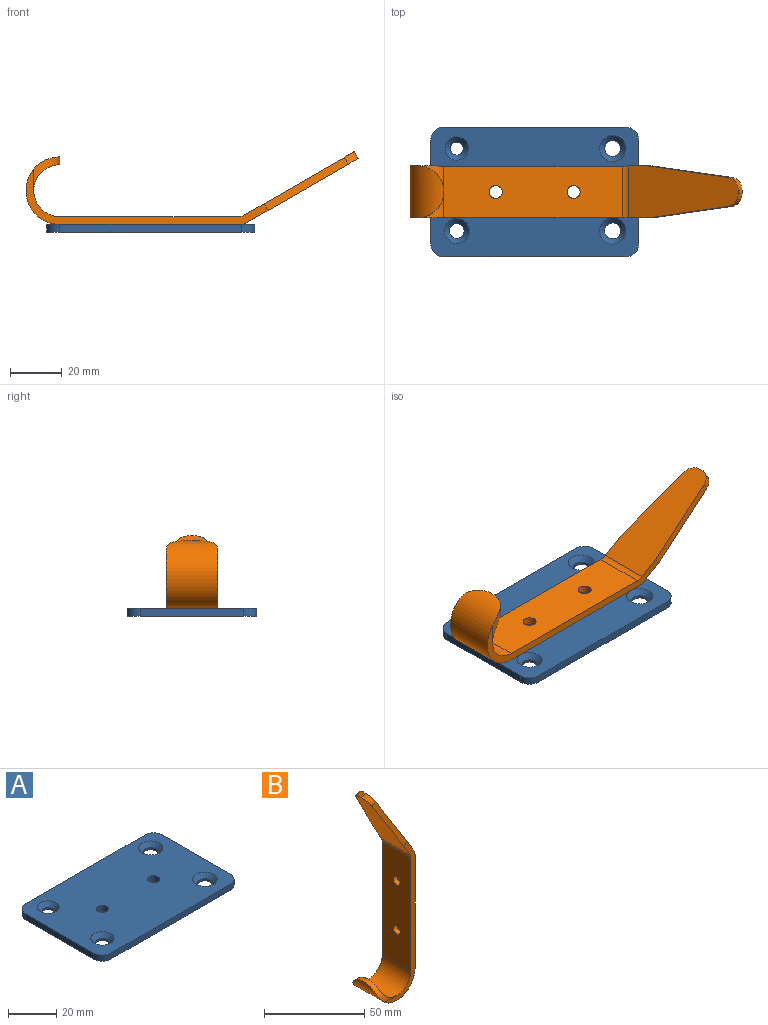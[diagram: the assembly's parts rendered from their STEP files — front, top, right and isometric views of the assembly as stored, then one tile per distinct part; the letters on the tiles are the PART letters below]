
ASSEMBLY  parts=2 mates=1
PART A: 20 faces, bbox 80x50x3 mm
  f0: plane 70x3mm, normal (0,1,0), area 210mm2, adj f4,f5,f6,f9
  f1: plane 40x3mm, normal (-1,0,0), area 120mm2, adj f4,f5,f6,f7
  f2: plane 70x3mm, normal (0,-1,0), area 210mm2, adj f4,f5,f7,f8
  f3: plane 40x3mm, normal (1,0,0), area 120mm2, adj f4,f5,f8,f9
  f4: plane 80x50mm, normal (0,0,1), area 3641.3mm2, adj f0,f1,f2,f3,f6,f7,f8,f9
  f5: plane 80x50mm, normal (0,0,-1), area 3835.5mm2, adj f0,f1,f2,f3,f6,f7,f8,f9
  f6: cylinder r=5mm len=5mm, axis (0,0,1), area 23.6mm2, adj f0,f1,f4,f5
  f7: cylinder r=5mm len=5mm, axis (0,0,-1), area 23.6mm2, adj f1,f2,f4,f5
  f8: cylinder r=5mm len=5mm, axis (0,0,1), area 23.6mm2, adj f2,f3,f4,f5
  f9: cylinder r=5mm len=5mm, axis (0,0,-1), area 23.6mm2, adj f0,f3,f4,f5
  f10: cylinder r=2.5mm len=5mm, axis (0,0,1), area 15.7mm2, adj f5,f17
  f11: cylinder r=3.08mm len=6.17mm, axis (0,0,1), area 19.4mm2, adj f5,f15
  f12: cylinder r=3.04mm len=6.08mm, axis (0,0,1), area 19.1mm2, adj f5,f14
  f13: cylinder r=2.83mm len=5.67mm, axis (0,0,1), area 17.8mm2, adj f5,f16
  f14: cone r=3.04mm half-angle=45deg, axis (0,0,1), area 71.8mm2, adj f4,f12
  f15: cone r=3.08mm half-angle=45deg, axis (0,0,1), area 72.6mm2, adj f4,f11
  f16: cone r=2.83mm half-angle=45deg, axis (0,0,1), area 68.1mm2, adj f4,f13
  f17: cone r=2.5mm half-angle=45deg, axis (0,0,1), area 62.2mm2, adj f4,f10
  f18: cylinder r=2.5mm len=5mm, axis (0,0,1), area 47.1mm2, adj f4,f5
  f19: cylinder r=2.5mm len=5mm, axis (0,0,1), area 47.1mm2, adj f4,f5
PART B: 18 faces, bbox 28x20x127.8 mm
  f0: cylinder r=13mm len=26mm, axis (0,1,0), area 772.6mm2, adj f1,f7,f8,f9
  f1: plane 69.46x20mm, normal (1,0,0), area 1350mm2, adj f0,f7,f8,f14,f15,f16
  f2: plane 42.84x24.73mm, normal (0.87,0,0.5), area 781.3mm2, adj f3,f7,f8,f10,f11,f12,f13,f16
  f3: plane 2.6x1.5mm, normal (-0.5,0,0.87), area 3.5mm2, adj f2,f4,f12,f13
  f4: plane 42.14x24.33mm, normal (-0.87,0,-0.5), area 765.2mm2, adj f3,f7,f8,f10,f11,f12,f13,f17
  f5: plane 68.66x20mm, normal (-1,0,0), area 1333.9mm2, adj f6,f7,f8,f14,f15,f17
  f6: cylinder r=10mm len=20mm, axis (0,1,0), area 582.9mm2, adj f5,f7,f8,f9
  f7: plane 93.16x21.31mm, normal (0,-1,0), area 313.6mm2, adj f0,f1,f2,f4,f5,f6,f9,f10
  f8: plane 93.16x21.31mm, normal (0,1,0), area 313.6mm2, adj f0,f1,f2,f4,f5,f6,f9,f11
  f9: cylinder r=10mm len=20mm, axis (1,0,0), area 109.2mm2, adj f0,f6,f7,f8
  f10: plane 32.35x20.41mm, normal (-0.06,-0.99,0.11), area 107.7mm2, adj f2,f4,f7,f12
  f11: plane 32.35x20.41mm, normal (-0.06,0.99,0.11), area 107.7mm2, adj f2,f4,f8,f13
  f12: cylinder r=5mm len=5.29mm, axis (-0.87,0,-0.5), area 21.7mm2, adj f2,f3,f4,f10
  f13: cylinder r=5mm len=5.29mm, axis (-0.87,0,-0.5), area 21.7mm2, adj f2,f3,f4,f11
  f14: cylinder r=2.5mm len=5mm, axis (-1,0,0), area 47.1mm2, adj f1,f5
  f15: cylinder r=2.5mm len=5mm, axis (-1,0,0), area 47.1mm2, adj f1,f5
  f16: cylinder r=5mm len=20mm, axis (0,1,0), area 52.4mm2, adj f1,f2,f7,f8
  f17: cylinder r=5mm len=20mm, axis (0,-1,0), area 52.4mm2, adj f4,f5,f7,f8
PLACE A t=(5.22,10.84,11.53)mm
PLACE B rot(axis=(0,1,0),90deg) t=(-30,21.58,27.53)mm
MATE fastened B.f15 <-> A.f18  axis (0,0,-1) through (20,11.58,14.53)mm
